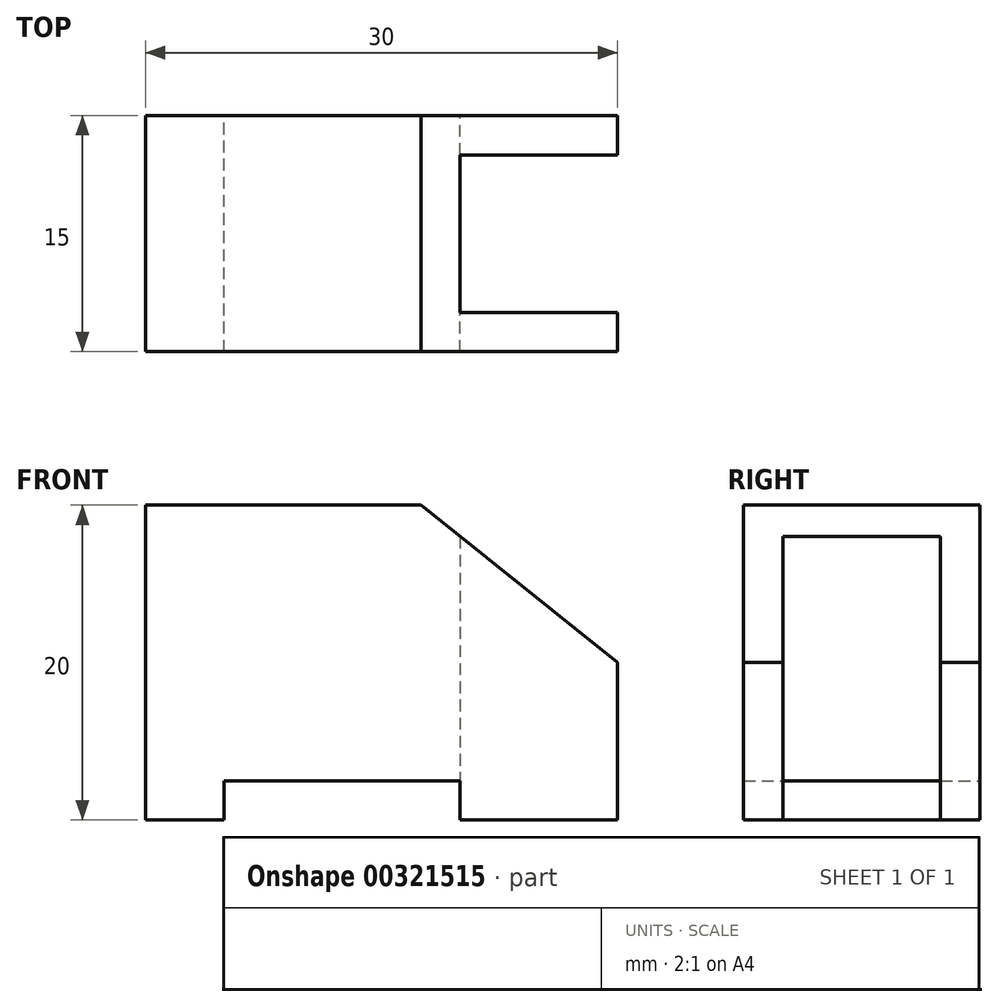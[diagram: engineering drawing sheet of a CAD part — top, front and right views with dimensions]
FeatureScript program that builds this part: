
annotation { "Feature Type Name" : "Feature", "Feature Type Description" : "" }
export const myFeature = defineFeature(function(context is Context, id is Id, definition is map)
    precondition{}
    {
        {
            var Q0;
            Q0=qCreatedBy(makeId("Front.planeOp"),FACE);
            var sketch = newSketch(context, id + "F0", { "sketchPlane" : qUnion([Q0])});
            skLineSegment(sketch, "E0", {"start": v(0, 0) * mm, "end": v(0, 20) * mm});
            skLineSegment(sketch, "E1", {"start": v(0, 20) * mm, "end": v(17.5, 20) * mm});
            skLineSegment(sketch, "E2", {"start": v(17.5, 20) * mm, "end": v(30, 10) * mm});
            skLineSegment(sketch, "E3", {"start": v(30, 10) * mm, "end": v(30, 0) * mm});
            skLineSegment(sketch, "E4", {"start": v(30, 0) * mm, "end": v(20, 0) * mm});
            skLineSegment(sketch, "E5", {"start": v(20, 0) * mm, "end": v(20, 2.5) * mm});
            skLineSegment(sketch, "E6", {"start": v(20, 2.5) * mm, "end": v(5, 2.5) * mm});
            skLineSegment(sketch, "E7", {"start": v(5, 2.5) * mm, "end": v(5, 0) * mm});
            skLineSegment(sketch, "E8", {"start": v(5, 0) * mm, "end": v(0, 0) * mm});
            skSolve(sketch);
        }
        {
            var Q0;
            Q0=makeQuery(id+"F0.imprint","IMPRINT",FACE,{"disambiguationData":[TD([[makeQuery(id+"F0.imprint","IMPRINT",EDGE,{"derivedFrom":sQuery(id+"F0.wireOp",EDGE,"E0")}),-1.0]])]});
            extrude(context, id + "F1", {"entities" : qUnion([Q0]), "depth" : 15 * mm});
        }
        {
            var Q0;
            Q0=qCreatedBy(makeId("Top.planeOp"),FACE);
            var sketch = newSketch(context, id + "F2", { "sketchPlane" : qUnion([Q0])});
            skLineSegment(sketch, "E9", {"start": v(30, -2.5) * mm, "end": v(20, -2.5) * mm});
            skLineSegment(sketch, "E10", {"start": v(20, -2.5) * mm, "end": v(20, -12.5) * mm});
            skLineSegment(sketch, "E11", {"start": v(20, -12.5) * mm, "end": v(30, -12.5) * mm});
            skLineSegment(sketch, "E12", {"start": v(30, -12.5) * mm, "end": v(30, -2.5) * mm});
            skSolve(sketch);
        }
        {
            var Q0;
            Q0 = qSketchRegion(id + "F2", true);
            extrude(context, id + "F3", {"entities" : qUnion([Q0]), "operationType" : NewBodyOperationType.REMOVE, "endBound" : BoundingType.THROUGH_ALL, "depth" : 25 * mm});
        }
    });
